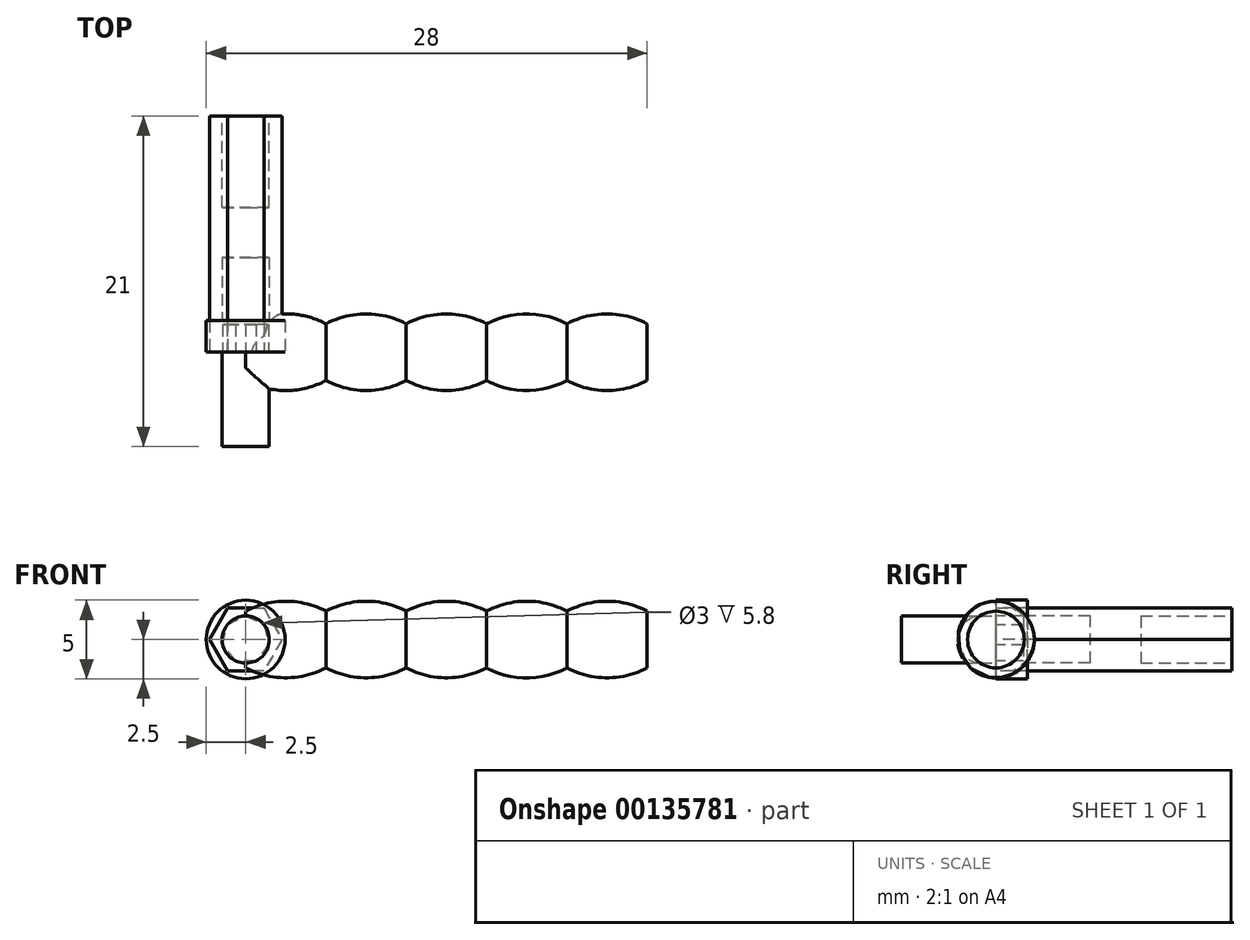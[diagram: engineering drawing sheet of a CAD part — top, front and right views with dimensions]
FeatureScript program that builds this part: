
annotation { "Feature Type Name" : "Feature", "Feature Type Description" : "" }
export const myFeature = defineFeature(function(context is Context, id is Id, definition is map)
    precondition{}
    {
        {
            var Q0;
            Q0=qCreatedBy(makeId("Front.planeOp"),FACE);
            var sketch = newSketch(context, id + "F0", { "sketchPlane" : qUnion([Q0])});
            skLineSegment(sketch, "E0", {"start": v(0, 0) * mm, "end": v(25.5, 0) * mm});
            skLineSegment(sketch, "E1", {"start": v(25.5, 0) * mm, "end": v(25.5, 1.8) * mm});
            skLineSegment(sketch, "E2", {"start": v(0, 0) * mm, "end": v(0, 1.8) * mm});
            skLineSegment(sketch, "E3", {"start": v(-10.3, 0) * mm, "end": v(46.8, 0) * mm, "construction": true});
            skLineSegment(sketch, "E4", {"start": v(-4.96, 1.8) * mm, "end": v(42.33, 1.8) * mm, "construction": true});
            skArc(sketch, "E5", {"start": v(5.1, 1.8) * mm, "mid": v(2.55, 2.43) * mm, "end": v(0, 1.8) * mm});
            skArc(sketch, "E6", {"start": v(10.2, 1.8) * mm, "mid": v(7.65, 2.43) * mm, "end": v(5.1, 1.8) * mm});
            skArc(sketch, "E7", {"start": v(15.3, 1.8) * mm, "mid": v(12.75, 2.43) * mm, "end": v(10.2, 1.8) * mm});
            skArc(sketch, "E8", {"start": v(20.4, 1.8) * mm, "mid": v(17.85, 2.43) * mm, "end": v(15.3, 1.8) * mm});
            skArc(sketch, "E9", {"start": v(25.5, 1.8) * mm, "mid": v(22.95, 2.43) * mm, "end": v(20.4, 1.8) * mm});
            skLineSegment(sketch, "E10", {"start": v(-3.95, -3) * mm, "end": v(34.52, -3) * mm, "construction": true});
            skSolve(sketch);
        }
        {
            var Q0;
            Q0 = qSketchRegion(id + "F0", true);
            var Q1;
            Q1=sQuery(id+"F0.wireOp",EDGE,"E3");
            revolve(context, id + "F1", {"entities" : qUnion([Q0]), "axis" : qUnion([Q1]), "revolveType" : RevolveType.FULL});
        }
        {
            var Q0;
            Q0=qCreatedBy(makeId("Front.planeOp"),FACE);
            var sketch = newSketch(context, id + "F2", { "sketchPlane" : qUnion([Q0])});
            skCircle(sketch, "E11.cCircle", {"center": v(0, 0) * mm, "radius": 2 * mm, "construction": true});
            skLineSegment(sketch, "E11.0", {"start": v(-2.3, 0) * mm, "end": v(-1.15, 2) * mm});
            skLineSegment(sketch, "E11.1", {"start": v(-1.15, 2) * mm, "end": v(1.15, 2) * mm});
            skLineSegment(sketch, "E11.2", {"start": v(1.15, 2) * mm, "end": v(2.3, 0) * mm});
            skLineSegment(sketch, "E11.3", {"start": v(2.3, 0) * mm, "end": v(1.15, -2) * mm});
            skLineSegment(sketch, "E11.4", {"start": v(1.15, -2) * mm, "end": v(-1.15, -2) * mm});
            skLineSegment(sketch, "E11.5", {"start": v(-1.15, -2) * mm, "end": v(-2.3, 0) * mm});
            skPoint(sketch, "E11.0.midPoint", {"position": v(-1.73, 1) * mm});
            skSolve(sketch);
        }
        {
            var Q0;
            Q0 = qSketchRegion(id + "F2", true);
            extrude(context, id + "F3", {"entities" : qUnion([Q0]), "oppositeDirection" : true, "depth" : 15 * mm});
        }
        {
            var Q0;
            Q0=makeQuery(id+"F3.opExtrude","CAP_FACE",FACE,{"disambiguationData":[OSD([sQuery(id+"F2.wireOp",EDGE,"E11.0"),sQuery(id+"F2.wireOp",EDGE,"E11.1"),sQuery(id+"F2.wireOp",EDGE,"E11.2"),sQuery(id+"F2.wireOp",EDGE,"E11.3"),sQuery(id+"F2.wireOp",EDGE,"E11.4"),sQuery(id+"F2.wireOp",EDGE,"E11.5")])],"isStart":true});
            var sketch = newSketch(context, id + "F4", { "sketchPlane" : qUnion([Q0])});
            skCircle(sketch, "E12", {"center": v(0, 0) * mm, "radius": 1.5 * mm});
            skSolve(sketch);
        }
        {
            var Q0;
            Q0=makeQuery(id+"F4.imprint","IMPRINT",FACE,{"disambiguationData":[TD([[makeQuery(id+"F4.imprint","IMPRINT",EDGE,{"derivedFrom":sQuery(id+"F4.wireOp",EDGE,"E12")}),1.0]])]});
            extrude(context, id + "F5", {"entities" : qUnion([Q0]), "operationType" : NewBodyOperationType.ADD, "depth" : 6 * mm});
        }
        {
            var Q0;
            Q0=qCreatedBy(makeId("Right.planeOp"),FACE);
            var sketch = newSketch(context, id + "F6", { "sketchPlane" : qUnion([Q0])});
            skLineSegment(sketch, "E13", {"start": v(-17.01, 0) * mm, "end": v(38.55, 0) * mm, "construction": true});
            skLineSegment(sketch, "E14", {"start": v(0, 0) * mm, "end": v(0, 2.5) * mm});
            skLineSegment(sketch, "E15", {"start": v(0, 2.5) * mm, "end": v(2, 2.5) * mm});
            skLineSegment(sketch, "E16", {"start": v(2, 2.5) * mm, "end": v(2, 1.5) * mm});
            skLineSegment(sketch, "E17", {"start": v(2, 1.5) * mm, "end": v(6, 1.5) * mm});
            skLineSegment(sketch, "E18", {"start": v(6, 1.5) * mm, "end": v(6, 0) * mm});
            skLineSegment(sketch, "E19", {"start": v(6, 0) * mm, "end": v(0, 0) * mm});
            skSolve(sketch);
        }
        {
            var Q0;
            Q0 = qSketchRegion(id + "F6", true);
            var Q1;
            Q1=sQuery(id+"F6.wireOp",EDGE,"E13");
            revolve(context, id + "F7", {"entities" : qUnion([Q0]), "axis" : qUnion([Q1]), "revolveType" : RevolveType.FULL});
        }
        {
            var Q0;
            Q0=makeQuery(id+"F7.opRevolve","SWEPT_FACE",FACE,{"disambiguationData":[OSD([sQuery(id+"F6.wireOp",EDGE,"E14")])]});
            var sketch = newSketch(context, id + "F8", { "sketchPlane" : qUnion([Q0])});
            skCircle(sketch, "E20.cCircle", {"center": v(0, 0) * mm, "radius": 1.36 * mm, "construction": true});
            skLineSegment(sketch, "E20.0", {"start": v(0.65, -1.36) * mm, "end": v(-0.65, -1.36) * mm});
            skLineSegment(sketch, "E20.1", {"start": v(-0.65, -1.36) * mm, "end": v(-1.47, -0.34) * mm});
            skLineSegment(sketch, "E20.2", {"start": v(-1.47, -0.34) * mm, "end": v(-1.18, 0.94) * mm});
            skLineSegment(sketch, "E20.3", {"start": v(-1.18, 0.94) * mm, "end": v(0, 1.5) * mm});
            skLineSegment(sketch, "E20.4", {"start": v(0, 1.5) * mm, "end": v(1.18, 0.94) * mm});
            skLineSegment(sketch, "E20.5", {"start": v(1.18, 0.94) * mm, "end": v(1.47, -0.34) * mm});
            skLineSegment(sketch, "E20.6", {"start": v(1.47, -0.34) * mm, "end": v(0.65, -1.36) * mm});
            skPoint(sketch, "E20.0.midPoint", {"position": v(0, -1.36) * mm});
            skSolve(sketch);
        }
        {
            var Q0;
            Q0=makeQuery(id+"F8.imprint","IMPRINT",FACE,{"disambiguationData":[TD([[makeQuery(id+"F8.imprint","IMPRINT",EDGE,{"derivedFrom":sQuery(id+"F8.wireOp",EDGE,"E20.0")}),-1.0]])]});
            extrude(context, id + "F9", {"entities" : qUnion([Q0]), "operationType" : NewBodyOperationType.REMOVE, "oppositeDirection" : true, "depth" : 1.75 * mm});
        }
        {
            var Q0;
            Q0=makeQuery(id+"F3.opExtrude","CAP_FACE",FACE,{"disambiguationData":[OSD([sQuery(id+"F2.wireOp",EDGE,"E11.0"),sQuery(id+"F2.wireOp",EDGE,"E11.1"),sQuery(id+"F2.wireOp",EDGE,"E11.2"),sQuery(id+"F2.wireOp",EDGE,"E11.3"),sQuery(id+"F2.wireOp",EDGE,"E11.4"),sQuery(id+"F2.wireOp",EDGE,"E11.5")])],"isStart":false});
            var sketch = newSketch(context, id + "F10", { "sketchPlane" : qUnion([Q0])});
            skCircle(sketch, "E21", {"center": v(0, 0) * mm, "radius": 1.5 * mm});
            skSolve(sketch);
        }
        {
            var Q0;
            Q0=makeQuery(id+"F10.imprint","IMPRINT",FACE,{"disambiguationData":[TD([[makeQuery(id+"F10.imprint","IMPRINT",EDGE,{"derivedFrom":sQuery(id+"F10.wireOp",EDGE,"E21")}),1.0]])]});
            extrude(context, id + "F11", {"entities" : qUnion([Q0]), "operationType" : NewBodyOperationType.REMOVE, "oppositeDirection" : true, "depth" : 5.8 * mm});
        }
    });
